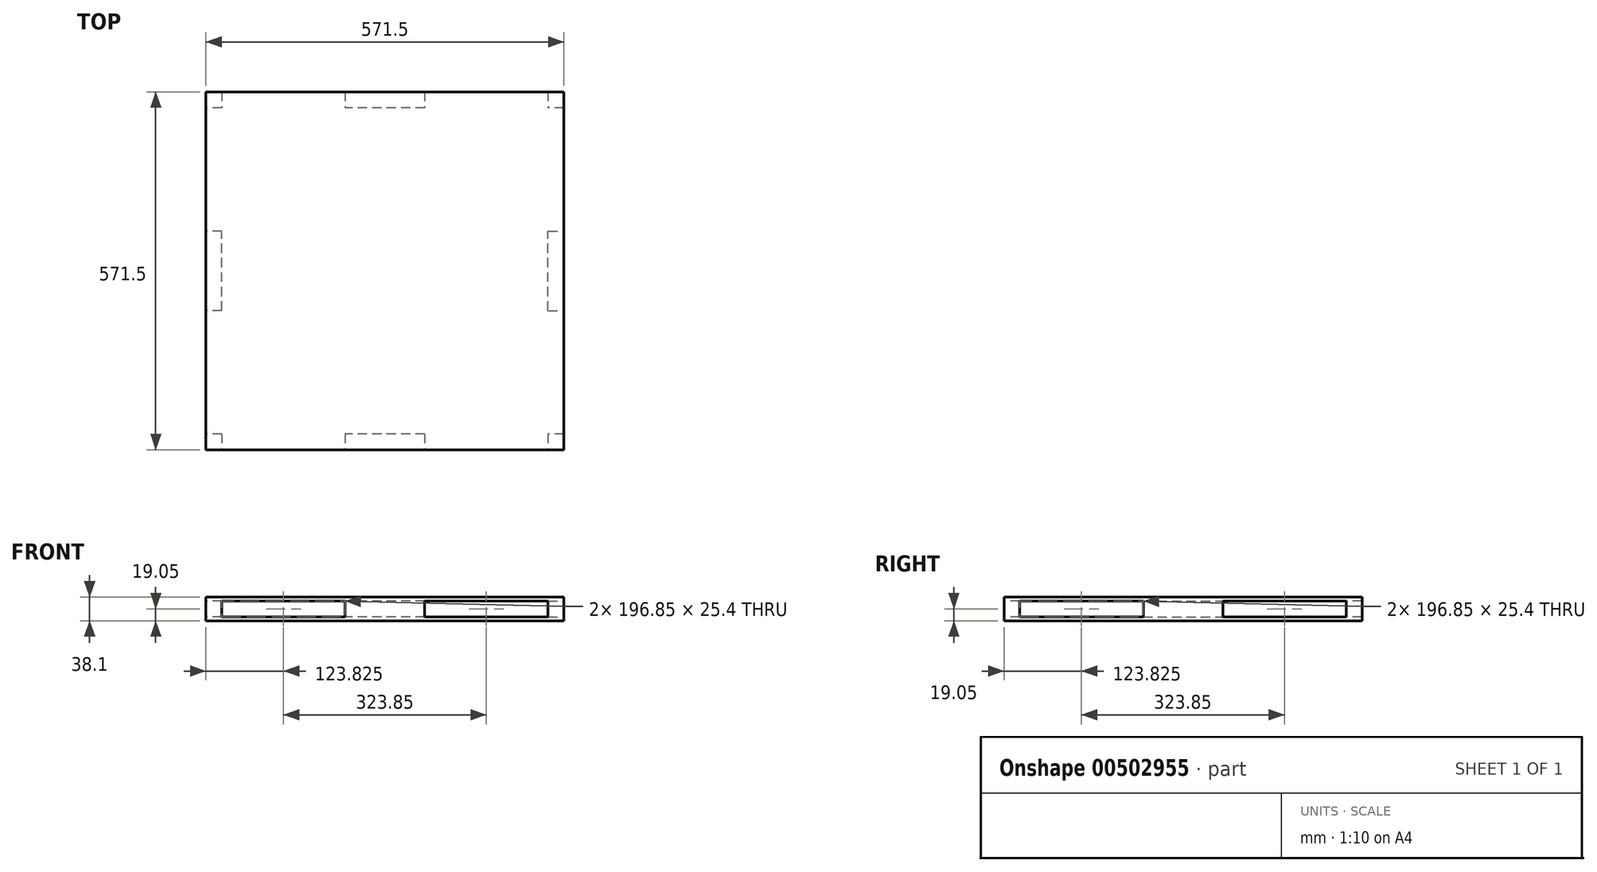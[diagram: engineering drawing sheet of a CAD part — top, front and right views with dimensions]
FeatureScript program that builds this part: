
annotation { "Feature Type Name" : "Feature", "Feature Type Description" : "" }
export const myFeature = defineFeature(function(context is Context, id is Id, definition is map)
    precondition{}
    {
        {
            var Q0;
            Q0=qCreatedBy(makeId("Top.planeOp"),FACE);
            var sketch = newSketch(context, id + "F0", { "sketchPlane" : qUnion([Q0])});
            skLineSegment(sketch, "E0.bottom", {"start": v(-285.75, 285.75) * mm, "end": v(285.75, 285.75) * mm});
            skLineSegment(sketch, "E0.top", {"start": v(-285.75, -285.75) * mm, "end": v(285.75, -285.75) * mm});
            skLineSegment(sketch, "E0.left", {"start": v(-285.75, 285.75) * mm, "end": v(-285.75, -285.75) * mm});
            skLineSegment(sketch, "E0.right", {"start": v(285.75, 285.75) * mm, "end": v(285.75, -285.75) * mm});
            skSolve(sketch);
        }
        {
            var Q0;
            Q0=makeQuery(id+"F0.imprint","IMPRINT",FACE,{"disambiguationData":[TD([[makeQuery(id+"F0.imprint","IMPRINT",EDGE,{"derivedFrom":sQuery(id+"F0.wireOp",EDGE,"E0.bottom")}),-1.0]])]});
            extrude(context, id + "F1", {"entities" : qUnion([Q0]), "depth" : 38.1 * mm});
        }
        {
            var Q0;
            Q0=makeQuery(id+"F1.opExtrude","SWEPT_FACE",FACE,{"disambiguationData":[OSD([sQuery(id+"F0.wireOp",EDGE,"E0.top")])]});
            var sketch = newSketch(context, id + "F2", { "sketchPlane" : qUnion([Q0])});
            skLineSegment(sketch, "E1", {"start": v(-260.35, 38.1) * mm, "end": v(-260.35, 0) * mm});
            skLineSegment(sketch, "E2", {"start": v(260.35, 38.1) * mm, "end": v(260.35, 0) * mm});
            skLineSegment(sketch, "E3", {"start": v(-63.5, 38.1) * mm, "end": v(-63.5, 0) * mm});
            skLineSegment(sketch, "E4", {"start": v(63.5, 38.1) * mm, "end": v(63.5, 0) * mm});
            skLineSegment(sketch, "E5", {"start": v(-260.35, 31.75) * mm, "end": v(-63.5, 31.75) * mm});
            skLineSegment(sketch, "E6", {"start": v(-260.35, 6.35) * mm, "end": v(-63.5, 6.35) * mm});
            skLineSegment(sketch, "E7", {"start": v(63.5, 31.75) * mm, "end": v(260.35, 31.75) * mm});
            skLineSegment(sketch, "E8", {"start": v(63.5, 6.35) * mm, "end": v(260.35, 6.35) * mm});
            skSolve(sketch);
        }
        {
            var Q0;
            {var subQ0=sQuery(id+"F2.wireOp",EDGE,"E5");Q0=makeQuery(id+"F2.imprint","IMPRINT",FACE,{"disambiguationData":[TD([[makeQuery(id+"F2.imprint","IMPRINT",EDGE,{"derivedFrom":subQ0}),-1.0]])]});}
            var Q1;
            {var subQ0=sQuery(id+"F2.wireOp",EDGE,"E7");Q1=makeQuery(id+"F2.imprint","IMPRINT",FACE,{"disambiguationData":[TD([[makeQuery(id+"F2.imprint","IMPRINT",EDGE,{"derivedFrom":subQ0}),-1.0]])]});}
            extrude(context, id + "F3", {"entities" : qUnion([Q0, Q1]), "operationType" : NewBodyOperationType.REMOVE, "endBound" : BoundingType.THROUGH_ALL, "oppositeDirection" : true, "depth" : 25.4 * mm});
        }
        {
            var Q0;
            Q0=makeQuery(id+"F1.opExtrude","SWEPT_FACE",FACE,{"disambiguationData":[OSD([sQuery(id+"F0.wireOp",EDGE,"E0.left")])]});
            var sketch = newSketch(context, id + "F4", { "sketchPlane" : qUnion([Q0])});
            skLineSegment(sketch, "E9", {"start": v(-260.35, 38.1) * mm, "end": v(-260.35, 0) * mm});
            skLineSegment(sketch, "E10", {"start": v(260.35, 38.1) * mm, "end": v(260.35, 0) * mm});
            skLineSegment(sketch, "E11", {"start": v(-260.35, 31.75) * mm, "end": v(260.35, 31.75) * mm});
            skLineSegment(sketch, "E12", {"start": v(-260.35, 6.35) * mm, "end": v(260.35, 6.35) * mm});
            skPoint(sketch, "E12.endSnap0", {"position": v(260.35, 19.05) * mm});
            skSolve(sketch);
        }
        {
            var Q0;
            {var subQ0=sQuery(id+"F4.wireOp",EDGE,"E11");Q0=makeQuery(id+"F4.imprint","IMPRINT",FACE,{"disambiguationData":[TD([[makeQuery(id+"F4.imprint","IMPRINT",EDGE,{"derivedFrom":subQ0}),-1.0]])]});}
            extrude(context, id + "F5", {"entities" : qUnion([Q0]), "operationType" : NewBodyOperationType.REMOVE, "endBound" : BoundingType.THROUGH_ALL, "oppositeDirection" : true, "depth" : 25.4 * mm});
        }
        {
            var Q0;
            Q0=makeQuery(id+"F1.opExtrude","CAP_FACE",FACE,{"disambiguationData":[OSD([sQuery(id+"F0.wireOp",EDGE,"E0.bottom"),sQuery(id+"F0.wireOp",EDGE,"E0.top"),sQuery(id+"F0.wireOp",EDGE,"E0.left"),sQuery(id+"F0.wireOp",EDGE,"E0.right")])],"isStart":false});
            var sketch = newSketch(context, id + "F6", { "sketchPlane" : qUnion([Q0])});
            skLineSegment(sketch, "E13.bottom", {"start": v(-285.75, 63.5) * mm, "end": v(-260.35, 63.5) * mm});
            skLineSegment(sketch, "E13.top", {"start": v(-285.75, -63.5) * mm, "end": v(-260.35, -63.5) * mm});
            skLineSegment(sketch, "E13.left", {"start": v(-285.75, 63.5) * mm, "end": v(-285.75, -63.5) * mm});
            skLineSegment(sketch, "E13.right", {"start": v(-260.35, 63.5) * mm, "end": v(-260.35, -63.5) * mm});
            skLineSegment(sketch, "E14.bottom", {"start": v(285.75, 63.5) * mm, "end": v(260.35, 63.5) * mm});
            skLineSegment(sketch, "E14.top", {"start": v(285.75, -63.5) * mm, "end": v(260.35, -63.5) * mm});
            skLineSegment(sketch, "E14.left", {"start": v(285.75, 63.5) * mm, "end": v(285.75, -63.5) * mm});
            skLineSegment(sketch, "E14.right", {"start": v(260.35, 63.5) * mm, "end": v(260.35, -63.5) * mm});
            skSolve(sketch);
        }
        {
            var Q0;
            Q0=makeQuery(id+"F6.imprint","IMPRINT",FACE,{"disambiguationData":[TD([[makeQuery(id+"F6.imprint","IMPRINT",EDGE,{"derivedFrom":sQuery(id+"F6.wireOp",EDGE,"E13.bottom")}),-1.0]])]});
            var Q1;
            Q1=makeQuery(id+"F6.imprint","IMPRINT",FACE,{"disambiguationData":[TD([[makeQuery(id+"F6.imprint","IMPRINT",EDGE,{"derivedFrom":sQuery(id+"F6.wireOp",EDGE,"E14.bottom")}),1.0]])]});
            extrude(context, id + "F7", {"entities" : qUnion([Q0, Q1]), "operationType" : NewBodyOperationType.ADD, "oppositeDirection" : true, "depth" : 38.1 * mm});
        }
    });
